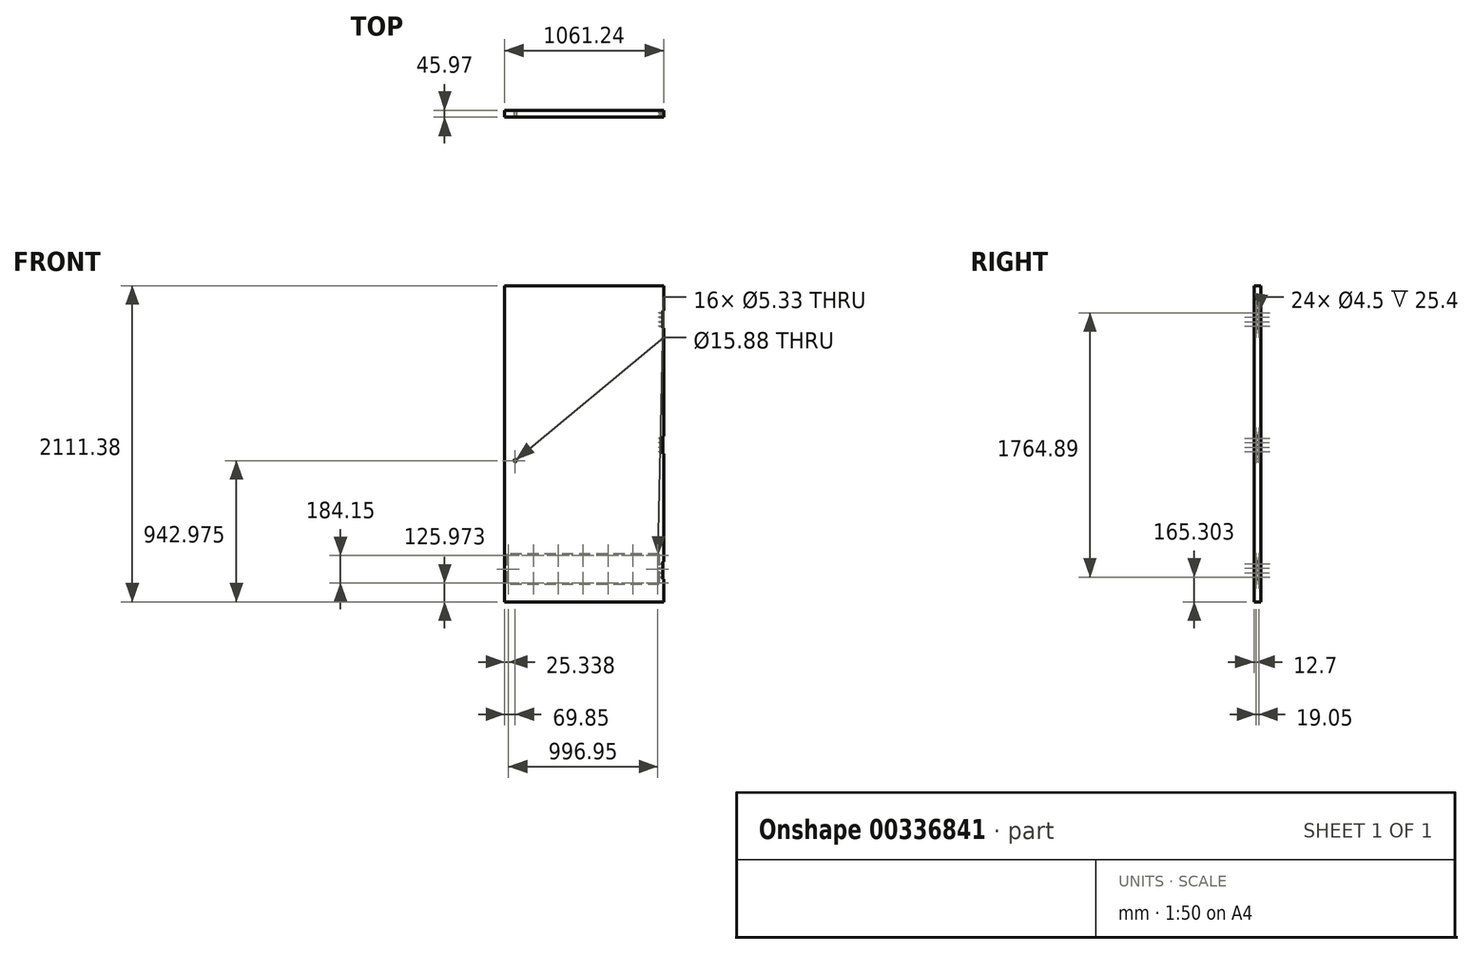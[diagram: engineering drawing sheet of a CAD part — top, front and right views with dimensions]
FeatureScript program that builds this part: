
annotation { "Feature Type Name" : "Feature", "Feature Type Description" : "" }
export const myFeature = defineFeature(function(context is Context, id is Id, definition is map)
    precondition{}
    {
        {
            var Q0;
            Q0=qCreatedBy(makeId("Front.planeOp"),FACE);
            var sketch = newSketch(context, id + "F0", { "sketchPlane" : qUnion([Q0])});
            skLineSegment(sketch, "E0.bottom", {"start": v(0, 0) * mm, "end": v(1061.24, 0) * mm});
            skLineSegment(sketch, "E0.top", {"start": v(0, 2111.38) * mm, "end": v(1061.24, 2111.38) * mm});
            skLineSegment(sketch, "E0.left", {"start": v(0, 0) * mm, "end": v(0, 2111.38) * mm});
            skLineSegment(sketch, "E0.right", {"start": v(1061.24, 0) * mm, "end": v(1061.24, 2111.38) * mm});
            skSolve(sketch);
        }
        {
            var Q0;
            Q0 = qSketchRegion(id + "F0", true);
            extrude(context, id + "F1", {"entities" : qUnion([Q0]), "depth" : 44.45 * mm});
        }
        {
            var Q0;
            Q0=qCreatedBy(makeId("Front.planeOp"),FACE);
            var sketch = newSketch(context, id + "F2", { "sketchPlane" : qUnion([Q0])});
            skLineSegment(sketch, "E1.0", {"start": v(1061.24, 0) * mm, "end": v(1061.24, 2111.38) * mm, "construction": true});
            skLineSegment(sketch, "E2.bottom", {"start": v(1061.24, 1943.9) * mm, "end": v(1056.67, 1943.9) * mm});
            skLineSegment(sketch, "E2.top", {"start": v(1061.24, 1828) * mm, "end": v(1056.67, 1828) * mm});
            skLineSegment(sketch, "E2.left", {"start": v(1061.24, 1943.9) * mm, "end": v(1061.24, 1828) * mm});
            skLineSegment(sketch, "E2.right", {"start": v(1056.67, 1943.9) * mm, "end": v(1056.67, 1828) * mm});
            skLineSegment(sketch, "E3.0.1.0", {"start": v(1061.24, 1105.7) * mm, "end": v(1056.67, 1105.7) * mm});
            skLineSegment(sketch, "E3.0.1.1", {"start": v(1061.24, 1105.7) * mm, "end": v(1061.24, 989.8) * mm});
            skLineSegment(sketch, "E3.0.1.2", {"start": v(1061.24, 989.8) * mm, "end": v(1056.67, 989.8) * mm});
            skLineSegment(sketch, "E3.0.1.3", {"start": v(1056.67, 1105.7) * mm, "end": v(1056.67, 989.8) * mm});
            skLineSegment(sketch, "E3.0.2.0", {"start": v(1061.24, 267.5) * mm, "end": v(1056.67, 267.5) * mm});
            skLineSegment(sketch, "E3.0.2.1", {"start": v(1061.24, 267.5) * mm, "end": v(1061.24, 151.6) * mm});
            skLineSegment(sketch, "E3.0.2.2", {"start": v(1061.24, 151.6) * mm, "end": v(1056.67, 151.6) * mm});
            skLineSegment(sketch, "E3.0.2.3", {"start": v(1056.67, 267.5) * mm, "end": v(1056.67, 151.6) * mm});
            skLineSegment(sketch, "E3.direction1", {"start": v(1056.67, 1943.9) * mm, "end": v(1082.07, 1943.9) * mm, "construction": true});
            skLineSegment(sketch, "E3.direction2", {"start": v(1056.67, 1943.9) * mm, "end": v(1056.67, 1105.7) * mm, "construction": true});
            skSolve(sketch);
        }
        {
            var Q0;
            Q0 = qSketchRegion(id + "F2", true);
            extrude(context, id + "F3", {"entities" : qUnion([Q0]), "operationType" : NewBodyOperationType.REMOVE, "endBound" : BoundingType.THROUGH_ALL, "depth" : 25.4 * mm});
        }
        {
            var Q0;
            Q0=makeQuery(id+"F3.boolean.opBoolean","COPY",FACE,{"derivedFrom":makeQuery(id+"F3.opExtrude","SWEPT_FACE",FACE,{"disambiguationData":[OSD([sQuery(id+"F2.wireOp",EDGE,"E2.right")])]})});
            var sketch = newSketch(context, id + "F4", { "sketchPlane" : qUnion([Q0])});
            skLineSegment(sketch, "E4.0.0", {"start": v(-44.45, 1828) * mm, "end": v(0, 1828) * mm, "construction": true});
            skLineSegment(sketch, "E4.0.1", {"start": v(0, 1828) * mm, "end": v(0, 1943.9) * mm, "construction": true});
            skLineSegment(sketch, "E4.0.2", {"start": v(0, 1943.9) * mm, "end": v(-44.45, 1943.9) * mm, "construction": true});
            skLineSegment(sketch, "E4.0.3", {"start": v(-44.45, 1943.9) * mm, "end": v(-44.45, 1828) * mm, "construction": true});
            skCircle(sketch, "E5", {"center": v(-31.75, 1930.2) * mm, "radius": 2.25 * mm});
            skCircle(sketch, "E6", {"center": v(-15.87, 1901.62) * mm, "radius": 2.25 * mm});
            skLineSegment(sketch, "E7", {"start": v(-44.45, 1885.95) * mm, "end": v(0, 1885.95) * mm, "construction": true});
            skLineSegment(sketch, "E8", {"start": v(-22.23, 1943.9) * mm, "end": v(-22.23, 1828) * mm, "construction": true});
            skCircle(sketch, "E9.MirrorC", {"center": v(-15.87, 1870.28) * mm, "radius": 2.25 * mm});
            skCircle(sketch, "E10.MirrorC", {"center": v(-31.75, 1841.7) * mm, "radius": 2.25 * mm});
            skCircle(sketch, "E11.MirrorC", {"center": v(-12.7, 1930.2) * mm, "radius": 2.25 * mm});
            skCircle(sketch, "E12.MirrorC", {"center": v(-28.57, 1901.62) * mm, "radius": 2.25 * mm});
            skCircle(sketch, "E13.MirrorC", {"center": v(-28.57, 1870.28) * mm, "radius": 2.25 * mm});
            skCircle(sketch, "E14.MirrorC", {"center": v(-12.7, 1841.7) * mm, "radius": 2.25 * mm});
            skLineSegment(sketch, "E15", {"start": v(0, 1954.23) * mm, "end": v(-6.35, 1954.23) * mm, "construction": true});
            skCircle(sketch, "E16.0.1.0", {"center": v(-31.75, 1092) * mm, "radius": 2.25 * mm});
            skCircle(sketch, "E16.0.1.1", {"center": v(-12.7, 1092) * mm, "radius": 2.25 * mm});
            skCircle(sketch, "E16.0.1.2", {"center": v(-15.87, 1063.42) * mm, "radius": 2.25 * mm});
            skCircle(sketch, "E16.0.1.3", {"center": v(-28.57, 1063.42) * mm, "radius": 2.25 * mm});
            skCircle(sketch, "E16.0.1.4", {"center": v(-15.87, 1032.08) * mm, "radius": 2.25 * mm});
            skCircle(sketch, "E16.0.1.5", {"center": v(-28.57, 1032.08) * mm, "radius": 2.25 * mm});
            skCircle(sketch, "E16.0.1.6", {"center": v(-12.7, 1003.5) * mm, "radius": 2.25 * mm});
            skCircle(sketch, "E16.0.1.7", {"center": v(-31.75, 1003.5) * mm, "radius": 2.25 * mm});
            skCircle(sketch, "E16.0.2.0", {"center": v(-31.75, 253.8) * mm, "radius": 2.25 * mm});
            skCircle(sketch, "E16.0.2.1", {"center": v(-12.7, 253.8) * mm, "radius": 2.25 * mm});
            skCircle(sketch, "E16.0.2.2", {"center": v(-15.87, 225.22) * mm, "radius": 2.25 * mm});
            skCircle(sketch, "E16.0.2.3", {"center": v(-28.57, 225.22) * mm, "radius": 2.25 * mm});
            skCircle(sketch, "E16.0.2.4", {"center": v(-15.87, 193.88) * mm, "radius": 2.25 * mm});
            skCircle(sketch, "E16.0.2.5", {"center": v(-28.57, 193.88) * mm, "radius": 2.25 * mm});
            skCircle(sketch, "E16.0.2.6", {"center": v(-12.7, 165.3) * mm, "radius": 2.25 * mm});
            skCircle(sketch, "E16.0.2.7", {"center": v(-31.75, 165.3) * mm, "radius": 2.25 * mm});
            skLineSegment(sketch, "E16.direction1", {"start": v(-31.75, 1930.2) * mm, "end": v(51.05, 1930.2) * mm, "construction": true});
            skLineSegment(sketch, "E16.direction2", {"start": v(-31.75, 1092) * mm, "end": v(-31.75, 1930.2) * mm, "construction": true});
            skSolve(sketch);
        }
        {
            var Q0;
            Q0 = qSketchRegion(id + "F4", true);
            extrude(context, id + "F5", {"entities" : qUnion([Q0]), "operationType" : NewBodyOperationType.REMOVE, "oppositeDirection" : true, "depth" : 25.4 * mm});
        }
        {
            var Q0;
            Q0=makeQuery(id+"F1.opExtrude","CAP_FACE",FACE,{"disambiguationData":[OSD([sQuery(id+"F0.wireOp",EDGE,"E0.bottom"),sQuery(id+"F0.wireOp",EDGE,"E0.top"),sQuery(id+"F0.wireOp",EDGE,"E0.left"),sQuery(id+"F0.wireOp",EDGE,"E0.right")])],"isStart":false});
            var sketch = newSketch(context, id + "F6", { "sketchPlane" : qUnion([Q0])});
            skCircle(sketch, "E17", {"center": v(69.85, 942.98) * mm, "radius": 7.94 * mm});
            skSolve(sketch);
        }
        {
            var Q0;
            Q0 = qSketchRegion(id + "F6", true);
            extrude(context, id + "F7", {"entities" : qUnion([Q0]), "operationType" : NewBodyOperationType.REMOVE, "endBound" : BoundingType.THROUGH_ALL, "oppositeDirection" : true, "depth" : 25.4 * mm});
        }
        {
            var Q0;
            Q0=makeQuery(id+"F1.opExtrude","CAP_FACE",FACE,{"disambiguationData":[OSD([sQuery(id+"F0.wireOp",EDGE,"E0.bottom"),sQuery(id+"F0.wireOp",EDGE,"E0.top"),sQuery(id+"F0.wireOp",EDGE,"E0.left"),sQuery(id+"F0.wireOp",EDGE,"E0.right")])],"isStart":true});
            var sketch = newSketch(context, id + "F8", { "sketchPlane" : qUnion([Q0])});
            skLineSegment(sketch, "E18.bottom", {"start": v(-1031.81, 319.65) * mm, "end": v(-15.81, 319.65) * mm});
            skLineSegment(sketch, "E18.top", {"start": v(-1031.81, 116.45) * mm, "end": v(-15.81, 116.45) * mm});
            skLineSegment(sketch, "E18.left", {"start": v(-1031.81, 319.65) * mm, "end": v(-1031.81, 116.45) * mm});
            skLineSegment(sketch, "E18.right", {"start": v(-15.81, 319.65) * mm, "end": v(-15.81, 116.45) * mm});
            skLineSegment(sketch, "E19.0", {"start": v(-1022.29, 310.12) * mm, "end": v(-25.34, 310.12) * mm, "construction": true});
            skLineSegment(sketch, "E19.1", {"start": v(-1022.29, 310.12) * mm, "end": v(-1022.29, 125.97) * mm, "construction": true});
            skLineSegment(sketch, "E19.2", {"start": v(-1022.29, 125.97) * mm, "end": v(-25.34, 125.97) * mm, "construction": true});
            skLineSegment(sketch, "E19.3", {"start": v(-25.34, 310.12) * mm, "end": v(-25.34, 125.97) * mm, "construction": true});
            skCircle(sketch, "E20", {"center": v(-1022.29, 310.12) * mm, "radius": 2.67 * mm});
            skCircle(sketch, "E21", {"center": v(-1022.29, 125.97) * mm, "radius": 2.67 * mm});
            skCircle(sketch, "E22", {"center": v(-25.34, 310.12) * mm, "radius": 2.67 * mm});
            skCircle(sketch, "E23", {"center": v(-25.34, 125.97) * mm, "radius": 2.67 * mm});
            skCircle(sketch, "E24", {"center": v(-523.81, 310.12) * mm, "radius": 2.67 * mm});
            skCircle(sketch, "E25", {"center": v(-523.81, 125.97) * mm, "radius": 2.67 * mm});
            skLineSegment(sketch, "E26", {"start": v(-1022.29, 310.12) * mm, "end": v(-856.13, 310.12) * mm, "construction": true});
            skLineSegment(sketch, "E27", {"start": v(-856.13, 310.12) * mm, "end": v(-689.97, 310.12) * mm, "construction": true});
            skLineSegment(sketch, "E28", {"start": v(-689.97, 310.12) * mm, "end": v(-523.81, 310.12) * mm, "construction": true});
            skCircle(sketch, "E29", {"center": v(-856.13, 310.12) * mm, "radius": 2.67 * mm});
            skCircle(sketch, "E30", {"center": v(-689.97, 310.12) * mm, "radius": 2.67 * mm});
            skCircle(sketch, "E31", {"center": v(-1022.29, 218.05) * mm, "radius": 2.67 * mm});
            skCircle(sketch, "E32", {"center": v(-25.34, 218.05) * mm, "radius": 2.67 * mm});
            skLineSegment(sketch, "E33", {"start": v(-523.81, 310.12) * mm, "end": v(-523.81, 125.97) * mm, "construction": true});
            skCircle(sketch, "E34.MirrorC", {"center": v(-357.65, 310.12) * mm, "radius": 2.67 * mm});
            skCircle(sketch, "E35.MirrorC", {"center": v(-191.5, 310.12) * mm, "radius": 2.67 * mm});
            skLineSegment(sketch, "E36", {"start": v(-523.81, 218.05) * mm, "end": v(-707.99, 218.05) * mm, "construction": true});
            skCircle(sketch, "E37.MirrorC", {"center": v(-856.13, 125.97) * mm, "radius": 2.67 * mm});
            skCircle(sketch, "E38.MirrorC", {"center": v(-689.97, 125.97) * mm, "radius": 2.67 * mm});
            skCircle(sketch, "E39.MirrorC", {"center": v(-357.65, 125.97) * mm, "radius": 2.67 * mm});
            skCircle(sketch, "E40.MirrorC", {"center": v(-191.5, 125.97) * mm, "radius": 2.67 * mm});
            skSolve(sketch);
        }
        {
            var Q0;
            Q0 = qSketchRegion(id + "F8", true);
            extrude(context, id + "F9", {"entities" : qUnion([Q0]), "depth" : 1.52 * mm});
        }
    });
